# Revit family: 10.Wichmann Akustikbox S_WAND
name_source: partatom
category: Mechanical Equipment
revit_build: Autodesk Revit 2018 (Build: 20170223_1515(x64)
units: mm (PartAtom-declared; Revit-internal decimal feet)

## family parameters
Always vertical = Yes
Classification = None
Cut with Voids When Loaded = No
Host = Wall
OmniClass Number = 23.30.20.00
OmniClass Title = Windows
Part Type = Normal
Room Calculation Point = No
Round Connector Dimension = Use Diameter
Shared = No

## types (5) — shared parameters
Bautiefe = 270 mm  [stored 0.885827 ft]
H_i = 65 mm
Höhe = 110 mm
Werkstoff = Stahl

## per-type parameters (varying)
| type | B_i | Breite | HAN |
| Akustikbox S, 110x280x270 mm, Innenöffnung 65x225x270 mm | 225 mm | 280 mm | ABS110280 |
| Akustikbox S, 110x335x270 mm, Innenöffnung 65x280x270 mm | 280 mm | 335 mm | ABS110335 |
| Akustikbox S, 110x435x270 mm, Innenöffnung 65x380x270 mm | 380 mm | 435 mm | ABS110435 |
| Akustikbox S, 110x535x270 mm, Innenöffnung 65x480x270 mm | 480 mm | 535 mm | ABS110535 |
| Akustikbox S, 110x640x270 mm, Innenöffnung 65x585x270 mm | 585 mm | 640 mm | ABS110640 |

note: [stored X ft] marks values corroborated as IEEE doubles in the binary element streams (Revit-internal decimal feet)

## geometry (parser evidence)
native form markers: Sweep x4
no freeform markers — native parametric forms only
